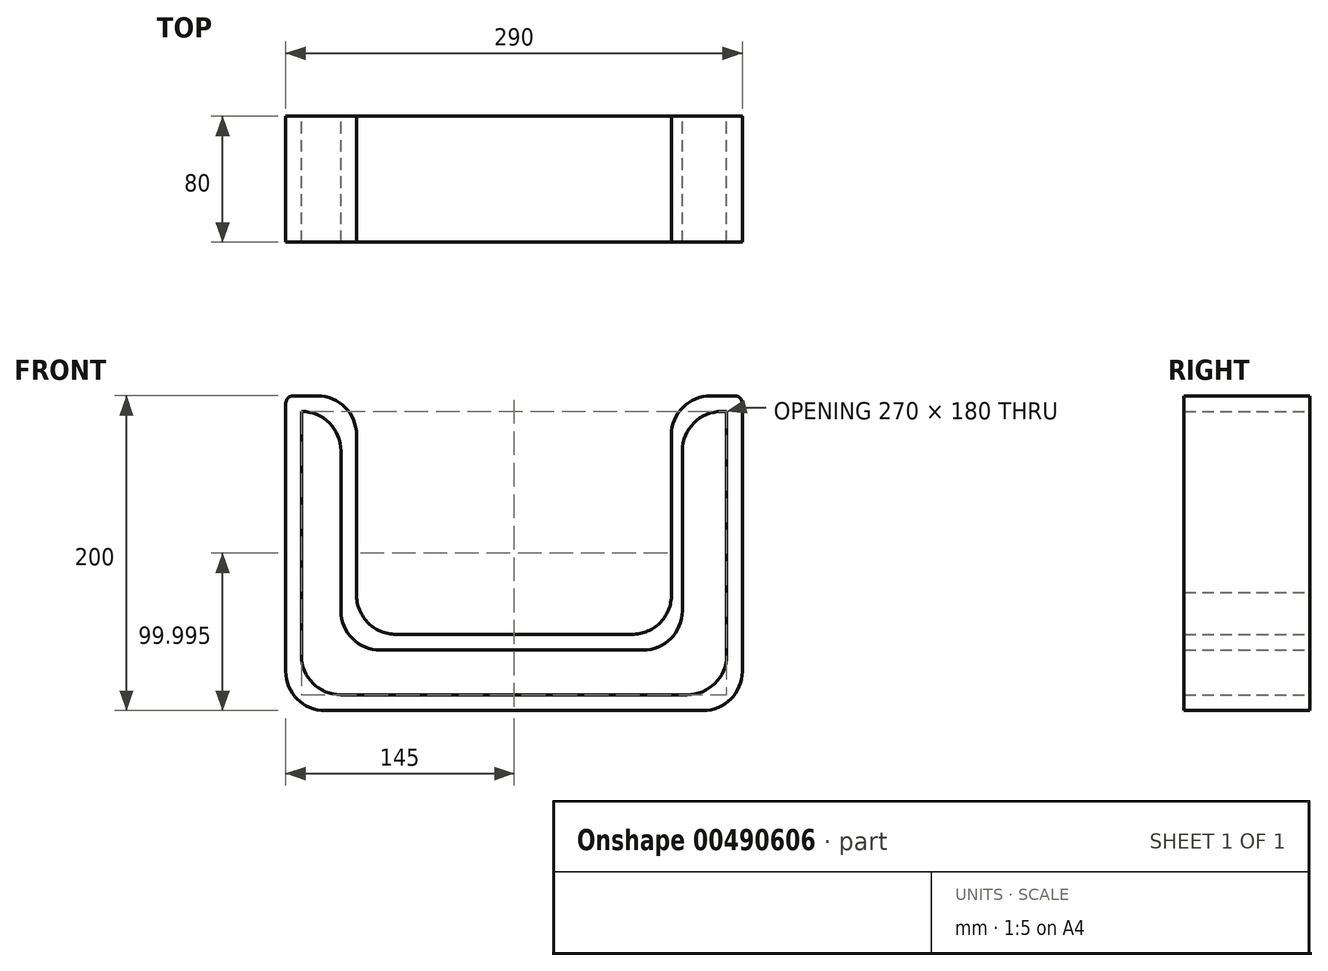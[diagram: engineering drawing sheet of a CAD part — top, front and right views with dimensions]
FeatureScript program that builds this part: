
annotation { "Feature Type Name" : "Feature", "Feature Type Description" : "" }
export const myFeature = defineFeature(function(context is Context, id is Id, definition is map)
    precondition{}
    {
        {
            var Q0;
            Q0=qCreatedBy(makeId("Front.planeOp"),FACE);
            var sketch = newSketch(context, id + "F0", { "sketchPlane" : qUnion([Q0])});
            skLineSegment(sketch, "E0", {"start": v(-75, 0) * mm, "end": v(75, 0) * mm});
            skArc(sketch, "E1", {"start": v(75, 0) * mm, "mid": v(93.22, 7.88) * mm, "end": v(99.95, 26.56) * mm});
            skLineSegment(sketch, "E2", {"start": v(0, 72.38) * mm, "end": v(0, -17.98) * mm});
            skArc(sketch, "E3.MirrorC", {"start": v(-75, 0) * mm, "mid": v(-93.22, 7.88) * mm, "end": v(-99.95, 26.56) * mm});
            skLineSegment(sketch, "E4", {"start": v(-125, 151.56) * mm, "end": v(-145, 151.56) * mm});
            skLineSegment(sketch, "E5", {"start": v(-145, 151.56) * mm, "end": v(-145, -23.44) * mm});
            skLineSegment(sketch, "E6", {"start": v(125, 151.56) * mm, "end": v(145, 151.56) * mm});
            skLineSegment(sketch, "E7", {"start": v(145, 151.56) * mm, "end": v(145, -23.44) * mm});
            skLineSegment(sketch, "E8", {"start": v(120, -48.44) * mm, "end": v(-120, -48.44) * mm});
            skLineSegment(sketch, "E9", {"start": v(-99.95, 26.56) * mm, "end": v(-100, 126.56) * mm});
            skLineSegment(sketch, "E10", {"start": v(100, 126.56) * mm, "end": v(99.95, 26.56) * mm});
            skLineSegment(sketch, "E11", {"start": v(-135, 141.56) * mm, "end": v(-134.95, 141.56) * mm});
            skLineSegment(sketch, "E12", {"start": v(-109.95, 116.56) * mm, "end": v(-109.95, 15) * mm});
            skLineSegment(sketch, "E13", {"start": v(-84.95, -10) * mm, "end": v(81.91, -10) * mm});
            skLineSegment(sketch, "E14", {"start": v(106.91, 15) * mm, "end": v(106.91, 116.56) * mm});
            skLineSegment(sketch, "E15", {"start": v(131.91, 141.56) * mm, "end": v(135, 141.56) * mm});
            skLineSegment(sketch, "E16", {"start": v(135, 141.56) * mm, "end": v(135, -13.44) * mm});
            skLineSegment(sketch, "E17", {"start": v(110, -38.44) * mm, "end": v(-110, -38.44) * mm});
            skLineSegment(sketch, "E18", {"start": v(-135, -13.44) * mm, "end": v(-135, 141.56) * mm});
            skPoint(sketch, "E19.visualSharp", {"position": v(-109.95, -10) * mm});
            skArc(sketch, "E19.filletArc", {"start": v(-109.95, 15) * mm, "mid": v(-102.63, -2.68) * mm, "end": v(-84.95, -10) * mm});
            skPoint(sketch, "E20.visualSharp", {"position": v(106.91, -10) * mm});
            skArc(sketch, "E20.filletArc", {"start": v(81.91, -10) * mm, "mid": v(99.6, -2.68) * mm, "end": v(106.91, 15) * mm});
            skPoint(sketch, "E21.visualSharp", {"position": v(-100, 151.56) * mm});
            skArc(sketch, "E21.filletArc", {"start": v(-100, 126.56) * mm, "mid": v(-107.32, 144.24) * mm, "end": v(-125, 151.56) * mm});
            skPoint(sketch, "E22.visualSharp", {"position": v(-109.95, 141.56) * mm});
            skArc(sketch, "E22.filletArc", {"start": v(-109.95, 116.56) * mm, "mid": v(-117.27, 134.23) * mm, "end": v(-134.95, 141.56) * mm});
            skPoint(sketch, "E23.visualSharp", {"position": v(100, 151.56) * mm});
            skArc(sketch, "E23.filletArc", {"start": v(125, 151.56) * mm, "mid": v(107.32, 144.24) * mm, "end": v(100, 126.56) * mm});
            skPoint(sketch, "E24.visualSharp", {"position": v(106.91, 141.56) * mm});
            skArc(sketch, "E24.filletArc", {"start": v(131.91, 141.56) * mm, "mid": v(114.24, 134.23) * mm, "end": v(106.91, 116.56) * mm});
            skPoint(sketch, "E25.visualSharp", {"position": v(-135, -38.44) * mm});
            skArc(sketch, "E25.filletArc", {"start": v(-135, -13.44) * mm, "mid": v(-127.68, -31.12) * mm, "end": v(-110, -38.44) * mm});
            skPoint(sketch, "E26.visualSharp", {"position": v(-145, -48.44) * mm});
            skArc(sketch, "E26.filletArc", {"start": v(-145, -23.44) * mm, "mid": v(-137.68, -41.12) * mm, "end": v(-120, -48.44) * mm});
            skPoint(sketch, "E27.visualSharp", {"position": v(135, -38.44) * mm});
            skArc(sketch, "E27.filletArc", {"start": v(110, -38.44) * mm, "mid": v(127.68, -31.12) * mm, "end": v(135, -13.44) * mm});
            skPoint(sketch, "E28.visualSharp", {"position": v(145, -48.44) * mm});
            skArc(sketch, "E28.filletArc", {"start": v(120, -48.44) * mm, "mid": v(137.68, -41.12) * mm, "end": v(145, -23.44) * mm});
            skSolve(sketch);
        }
        {
            var Q0;
            {var subQ5=sQuery(id+"F0.wireOp",EDGE,"E1");Q0=makeQuery(id+"F0.imprint","IMPRINT",FACE,{"disambiguationData":[TD([[makeQuery(id+"F0.imprint","IMPRINT",EDGE,{"derivedFrom":subQ5}),-1.0]])]});}
            extrude(context, id + "F1", {"entities" : qUnion([Q0]), "endBound" : BoundingType.SYMMETRIC, "depth" : 80 * mm});
        }
        {
            var Q0;
            Q0=makeQuery(id+"F1.opExtrude","SWEPT_EDGE",EDGE,{"disambiguationData":[OSD([sQuery(id+"F0.wireOp",EDGE,"E4"),sQuery(id+"F0.wireOp",EDGE,"E5")])]});
            var Q1;
            Q1=makeQuery(id+"F1.opExtrude","SWEPT_EDGE",EDGE,{"disambiguationData":[OSD([sQuery(id+"F0.wireOp",EDGE,"E6"),sQuery(id+"F0.wireOp",EDGE,"E7")])]});
            fillet(context, id + "F2", {"entities" : qUnion([Q0, Q1]), "radius" : 5 * mm, "tangentPropagation" : true, "allowEdgeOverflow" : false});
        }
    });
